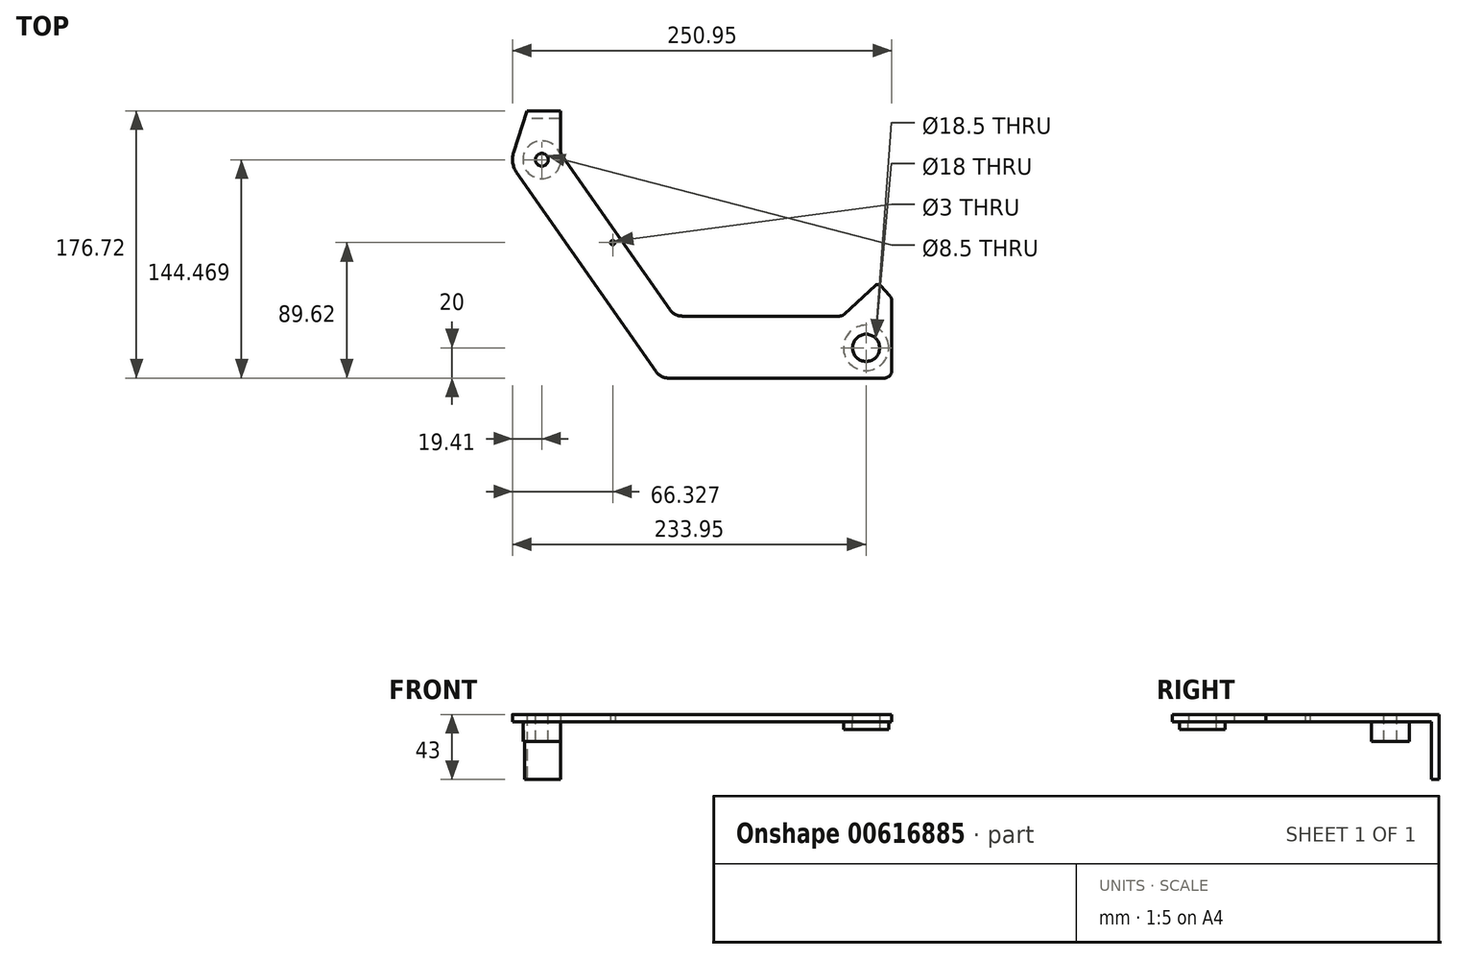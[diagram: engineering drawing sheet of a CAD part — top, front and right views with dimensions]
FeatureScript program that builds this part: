
annotation { "Feature Type Name" : "Feature", "Feature Type Description" : "" }
export const myFeature = defineFeature(function(context is Context, id is Id, definition is map)
    precondition{}
    {
        {
            var Q0;
            Q0=qCreatedBy(makeId("Top.planeOp"),FACE);
            var sketch = newSketch(context, id + "F0", { "sketchPlane" : qUnion([Q0])});
            skLineSegment(sketch, "E0", {"start": v(-5, 0) * mm, "end": v(-147.8, 0) * mm});
            skLineSegment(sketch, "E1", {"start": v(-155.99, 4.26) * mm, "end": v(-248.24, 136.01) * mm});
            skLineSegment(sketch, "E2", {"start": v(-250.21, 149.25) * mm, "end": v(-241.29, 176.72) * mm});
            skLineSegment(sketch, "E3", {"start": v(-241.29, 176.72) * mm, "end": v(-219.29, 176.72) * mm});
            skLineSegment(sketch, "E4", {"start": v(-219.29, 176.72) * mm, "end": v(-219.29, 151.87) * mm});
            skLineSegment(sketch, "E5", {"start": v(-217.48, 146.14) * mm, "end": v(-146.85, 45.26) * mm});
            skLineSegment(sketch, "E6", {"start": v(-138.66, 41) * mm, "end": v(-34.73, 41) * mm});
            skLineSegment(sketch, "E7", {"start": v(-7.5, 61.13) * mm, "end": v(-1.34, 54.53) * mm});
            skLineSegment(sketch, "E8", {"start": v(0, 51.12) * mm, "end": v(0, 5) * mm});
            skPoint(sketch, "E9.visualSharp", {"position": v(-252.53, 142.14) * mm});
            skArc(sketch, "E9.filletArc", {"start": v(-250.21, 149.25) * mm, "mid": v(-250.78, 142.4) * mm, "end": v(-248.24, 136.01) * mm});
            skPoint(sketch, "E10.visualSharp", {"position": v(-153, 0) * mm});
            skArc(sketch, "E10.filletArc", {"start": v(-155.99, 4.26) * mm, "mid": v(-152.41, 1.13) * mm, "end": v(-147.8, 0) * mm});
            skPoint(sketch, "E11.visualSharp", {"position": v(0, 0) * mm});
            skArc(sketch, "E11.filletArc", {"start": v(-5, 0) * mm, "mid": v(-1.46, 1.46) * mm, "end": v(0, 5) * mm});
            skPoint(sketch, "E12.visualSharp", {"position": v(0, 53.09) * mm});
            skArc(sketch, "E12.filletArc", {"start": v(0, 51.12) * mm, "mid": v(-0.35, 52.95) * mm, "end": v(-1.34, 54.53) * mm});
            skPoint(sketch, "E13.visualSharp", {"position": v(-143.86, 41) * mm});
            skArc(sketch, "E13.filletArc", {"start": v(-146.85, 45.26) * mm, "mid": v(-143.28, 42.13) * mm, "end": v(-138.66, 41) * mm});
            skPoint(sketch, "E14.visualSharp", {"position": v(-219.29, 148.72) * mm});
            skArc(sketch, "E14.filletArc", {"start": v(-219.29, 151.87) * mm, "mid": v(-218.83, 148.86) * mm, "end": v(-217.48, 146.14) * mm});
            skCircle(sketch, "E15", {"center": v(-17, 20) * mm, "radius": 9 * mm});
            skCircle(sketch, "E16", {"center": v(-231.54, 144.47) * mm, "radius": 4.25 * mm, "construction": true});
            skCircle(sketch, "E17", {"center": v(-231.54, 144.47) * mm, "radius": 12.5 * mm, "construction": true});
            skCircle(sketch, "E18", {"center": v(-184.62, 89.62) * mm, "radius": 1.5 * mm});
            skLineSegment(sketch, "E19", {"start": v(-184.62, 89.62) * mm, "end": v(-180.12, 92.78) * mm, "construction": true});
            skLineSegment(sketch, "E20", {"start": v(-11.04, 61.26) * mm, "end": v(-31.32, 42.34) * mm});
            skPoint(sketch, "E21.visualSharp", {"position": v(-9.2, 62.96) * mm});
            skArc(sketch, "E21.filletArc", {"start": v(-7.5, 61.13) * mm, "mid": v(-9.24, 61.93) * mm, "end": v(-11.04, 61.26) * mm});
            skPoint(sketch, "E22.visualSharp", {"position": v(-32.76, 41) * mm});
            skArc(sketch, "E22.filletArc", {"start": v(-34.73, 41) * mm, "mid": v(-32.9, 41.35) * mm, "end": v(-31.32, 42.34) * mm});
            skCircle(sketch, "E23", {"center": v(-226.88, 144.47) * mm, "radius": 32.25 * mm, "construction": true});
            skLineSegment(sketch, "E24", {"start": v(-231.54, 144.47) * mm, "end": v(-166.95, 144.47) * mm, "construction": true});
            skSolve(sketch);
        }
        {
            var Q0;
            Q0 = qSketchRegion(id + "F0", true);
            extrude(context, id + "F1", {"entities" : qUnion([Q0]), "depth" : 5 * mm, "offsetDistance" : 25 * mm});
        }
        {
            var Q0;
            Q0=makeQuery(id+"F1.opExtrude","CAP_FACE",FACE,{"disambiguationData":[OSD([sQuery(id+"F0.wireOp",EDGE,"E0"),sQuery(id+"F0.wireOp",EDGE,"E1"),sQuery(id+"F0.wireOp",EDGE,"E2"),sQuery(id+"F0.wireOp",EDGE,"E3"),sQuery(id+"F0.wireOp",EDGE,"E4"),sQuery(id+"F0.wireOp",EDGE,"E5"),sQuery(id+"F0.wireOp",EDGE,"E6"),sQuery(id+"F0.wireOp",EDGE,"AKJhnsKv-fRIL-mSII-hMqQ-wiGmtFYKsOxh"),sQuery(id+"F0.wireOp",EDGE,"E7"),sQuery(id+"F0.wireOp",EDGE,"E8"),sQuery(id+"F0.wireOp",EDGE,"E9.filletArc"),sQuery(id+"F0.wireOp",EDGE,"E10.filletArc"),sQuery(id+"F0.wireOp",EDGE,"E11.filletArc"),sQuery(id+"F0.wireOp",EDGE,"c0c80081-755d-4ee6-b2f2-95969b86fadd.filletArc"),sQuery(id+"F0.wireOp",EDGE,"548059d1-6878-4f95-b68c-bbc5d665af0b.filletArc"),sQuery(id+"F0.wireOp",EDGE,"E12.filletArc"),sQuery(id+"F0.wireOp",EDGE,"E13.filletArc"),sQuery(id+"F0.wireOp",EDGE,"E14.filletArc"),sQuery(id+"F0.wireOp",EDGE,"E15"),sQuery(id+"F0.wireOp",EDGE,"E18")])],"isStart":true});
            var sketch = newSketch(context, id + "F2", { "sketchPlane" : qUnion([Q0])});
            skLineSegment(sketch, "E25.0", {"start": v(-241.29, -176.72) * mm, "end": v(-219.29, -176.72) * mm});
            skLineSegment(sketch, "E26.0", {"start": v(-219.29, -176.72) * mm, "end": v(-219.29, -171.72) * mm});
            skLineSegment(sketch, "E27.0", {"start": v(-242.91, -171.72) * mm, "end": v(-241.29, -176.72) * mm});
            skLineSegment(sketch, "E28", {"start": v(-219.29, -171.72) * mm, "end": v(-242.91, -171.72) * mm});
            skSolve(sketch);
        }
        {
            var Q0;
            Q0 = qSketchRegion(id + "F2", true);
            extrude(context, id + "F3", {"entities" : qUnion([Q0]), "operationType" : NewBodyOperationType.ADD, "depth" : 38 * mm, "offsetDistance" : 25 * mm});
        }
        {
            var Q0;
            Q0=makeQuery(id+"F0.imprint","IMPRINT",FACE,{"disambiguationData":[TD([[makeQuery(id+"F0.imprint","IMPRINT",EDGE,{"derivedFrom":sQuery(id+"F0.wireOp",EDGE,"E0")}),-1.0]])]});
            var sketch = newSketch(context, id + "F4", { "sketchPlane" : qUnion([Q0])});
            skCircle(sketch, "E29.0", {"center": v(-231.54, 144.47) * mm, "radius": 12.5 * mm});
            skSolve(sketch);
        }
        {
            var Q0;
            Q0 = qSketchRegion(id + "F4", true);
            extrude(context, id + "F5", {"entities" : qUnion([Q0]), "operationType" : NewBodyOperationType.ADD, "oppositeDirection" : true, "depth" : 13 * mm, "offsetDistance" : 25 * mm});
        }
        {
            var Q0;
            Q0=makeQuery(id+"F1.opExtrude","CAP_FACE",FACE,{"disambiguationData":[OSD([sQuery(id+"F0.wireOp",EDGE,"E0"),sQuery(id+"F0.wireOp",EDGE,"E1"),sQuery(id+"F0.wireOp",EDGE,"E2"),sQuery(id+"F0.wireOp",EDGE,"E3"),sQuery(id+"F0.wireOp",EDGE,"E4"),sQuery(id+"F0.wireOp",EDGE,"E5"),sQuery(id+"F0.wireOp",EDGE,"E6"),sQuery(id+"F0.wireOp",EDGE,"AKJhnsKv-fRIL-mSII-hMqQ-wiGmtFYKsOxh"),sQuery(id+"F0.wireOp",EDGE,"E7"),sQuery(id+"F0.wireOp",EDGE,"E8"),sQuery(id+"F0.wireOp",EDGE,"E9.filletArc"),sQuery(id+"F0.wireOp",EDGE,"E10.filletArc"),sQuery(id+"F0.wireOp",EDGE,"E11.filletArc"),sQuery(id+"F0.wireOp",EDGE,"c0c80081-755d-4ee6-b2f2-95969b86fadd.filletArc"),sQuery(id+"F0.wireOp",EDGE,"548059d1-6878-4f95-b68c-bbc5d665af0b.filletArc"),sQuery(id+"F0.wireOp",EDGE,"E12.filletArc"),sQuery(id+"F0.wireOp",EDGE,"E13.filletArc"),sQuery(id+"F0.wireOp",EDGE,"E14.filletArc"),sQuery(id+"F0.wireOp",EDGE,"E15"),sQuery(id+"F0.wireOp",EDGE,"E18")])],"isStart":false});
            var sketch = newSketch(context, id + "F6", { "sketchPlane" : qUnion([Q0])});
            skCircle(sketch, "E30.0", {"center": v(-231.54, 144.47) * mm, "radius": 4.25 * mm});
            skSolve(sketch);
        }
        {
            var Q0;
            Q0=makeQuery(id+"F6.imprint","IMPRINT",FACE,{"disambiguationData":[TD([[makeQuery(id+"F6.imprint","IMPRINT",EDGE,{"derivedFrom":sQuery(id+"F6.wireOp",EDGE,"E30.0")}),1.0]])]});
            extrude(context, id + "F7", {"entities" : qUnion([Q0]), "operationType" : NewBodyOperationType.REMOVE, "endBound" : BoundingType.THROUGH_ALL, "oppositeDirection" : true, "depth" : 25 * mm, "offsetDistance" : 25 * mm});
        }
        {
            var Q0;
            Q0=makeQuery(id+"F1.opExtrude","CAP_FACE",FACE,{"disambiguationData":[OSD([sQuery(id+"F0.wireOp",EDGE,"E0"),sQuery(id+"F0.wireOp",EDGE,"E1"),sQuery(id+"F0.wireOp",EDGE,"E2"),sQuery(id+"F0.wireOp",EDGE,"E3"),sQuery(id+"F0.wireOp",EDGE,"E4"),sQuery(id+"F0.wireOp",EDGE,"E5"),sQuery(id+"F0.wireOp",EDGE,"E6"),sQuery(id+"F0.wireOp",EDGE,"E7"),sQuery(id+"F0.wireOp",EDGE,"E8"),sQuery(id+"F0.wireOp",EDGE,"E9.filletArc"),sQuery(id+"F0.wireOp",EDGE,"E10.filletArc"),sQuery(id+"F0.wireOp",EDGE,"E11.filletArc"),sQuery(id+"F0.wireOp",EDGE,"E12.filletArc"),sQuery(id+"F0.wireOp",EDGE,"E13.filletArc"),sQuery(id+"F0.wireOp",EDGE,"E14.filletArc"),sQuery(id+"F0.wireOp",EDGE,"E15"),sQuery(id+"F0.wireOp",EDGE,"E18"),sQuery(id+"F0.wireOp",EDGE,"E20")])],"isStart":true});
            var sketch = newSketch(context, id + "F8", { "sketchPlane" : qUnion([Q0])});
            skCircle(sketch, "E31", {"center": v(-17, -20) * mm, "radius": 15 * mm});
            skCircle(sketch, "E32.0", {"center": v(-17, -20) * mm, "radius": 9 * mm, "construction": true});
            skCircle(sketch, "E33", {"center": v(-17, -20) * mm, "radius": 9.25 * mm});
            skSolve(sketch);
        }
        {
            var Q0;
            Q0 = qSketchRegion(id + "F8", true);
            extrude(context, id + "F9", {"entities" : qUnion([Q0]), "depth" : 5 * mm, "offsetDistance" : 25 * mm});
        }
    });
